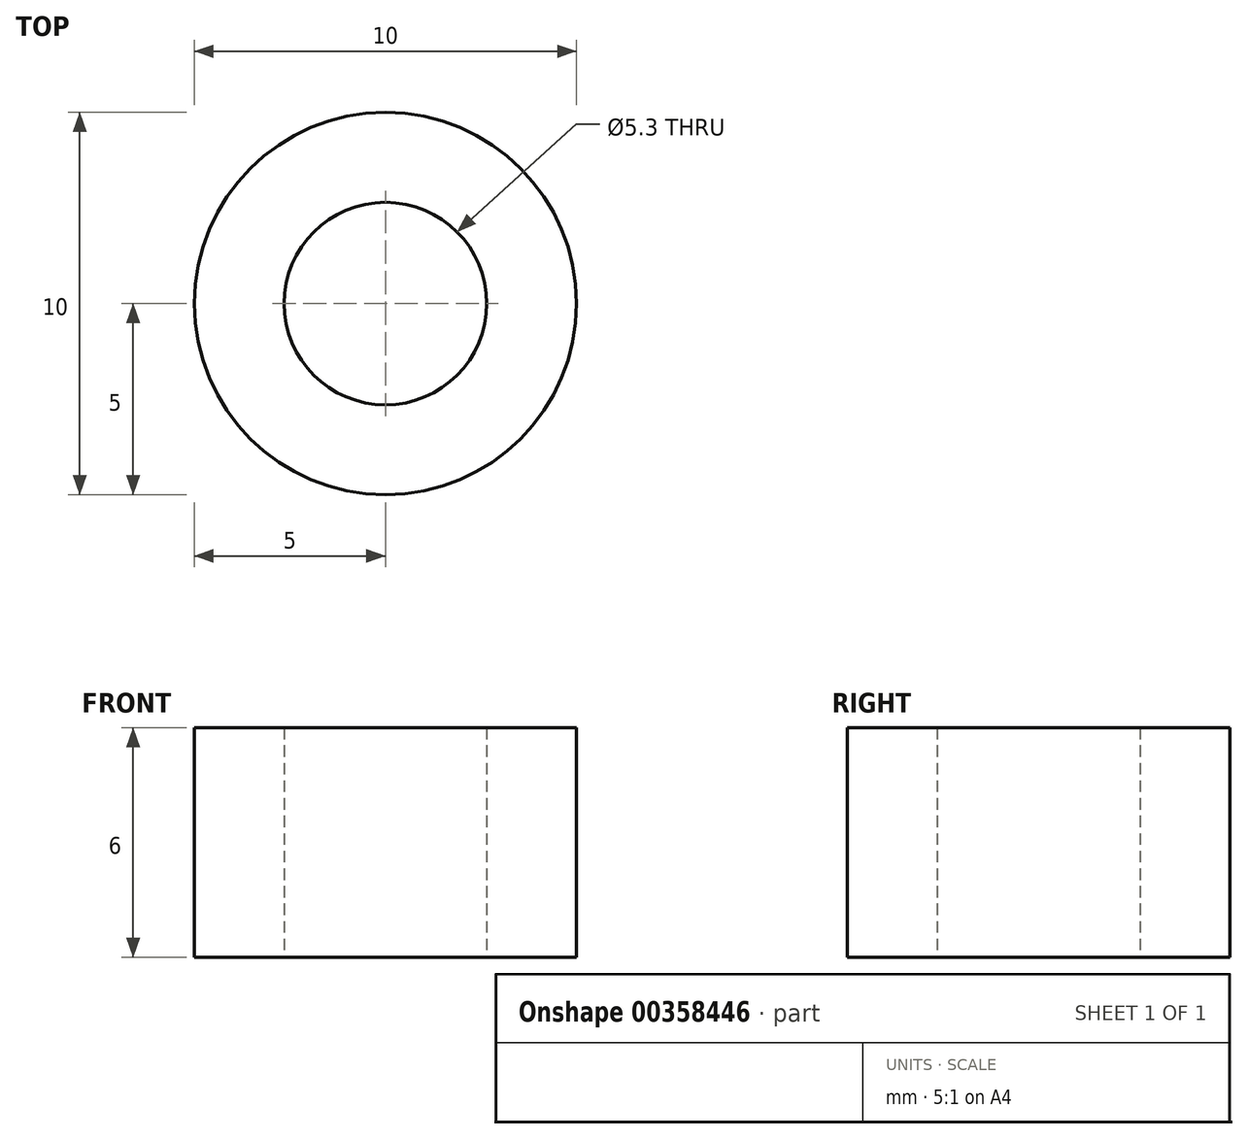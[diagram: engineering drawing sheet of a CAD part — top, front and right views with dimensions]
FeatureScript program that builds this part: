
annotation { "Feature Type Name" : "Feature", "Feature Type Description" : "" }
export const myFeature = defineFeature(function(context is Context, id is Id, definition is map)
    precondition{}
    {
        {
            var Q0;
            Q0=qCreatedBy(makeId("Top.planeOp"),FACE);
            var sketch = newSketch(context, id + "F0", { "sketchPlane" : qUnion([Q0])});
            skCircle(sketch, "E0", {"center": v(0, 0) * mm, "radius": 2.65 * mm});
            skCircle(sketch, "E1", {"center": v(0, 0) * mm, "radius": 5 * mm});
            skSolve(sketch);
        }
        {
            var Q0;
            Q0=qSketchRegion(id+"F0",true);
            extrude(context, id + "F1", {"entities" : qUnion([Q0]), "depth" : 6 * mm});
        }
    });
